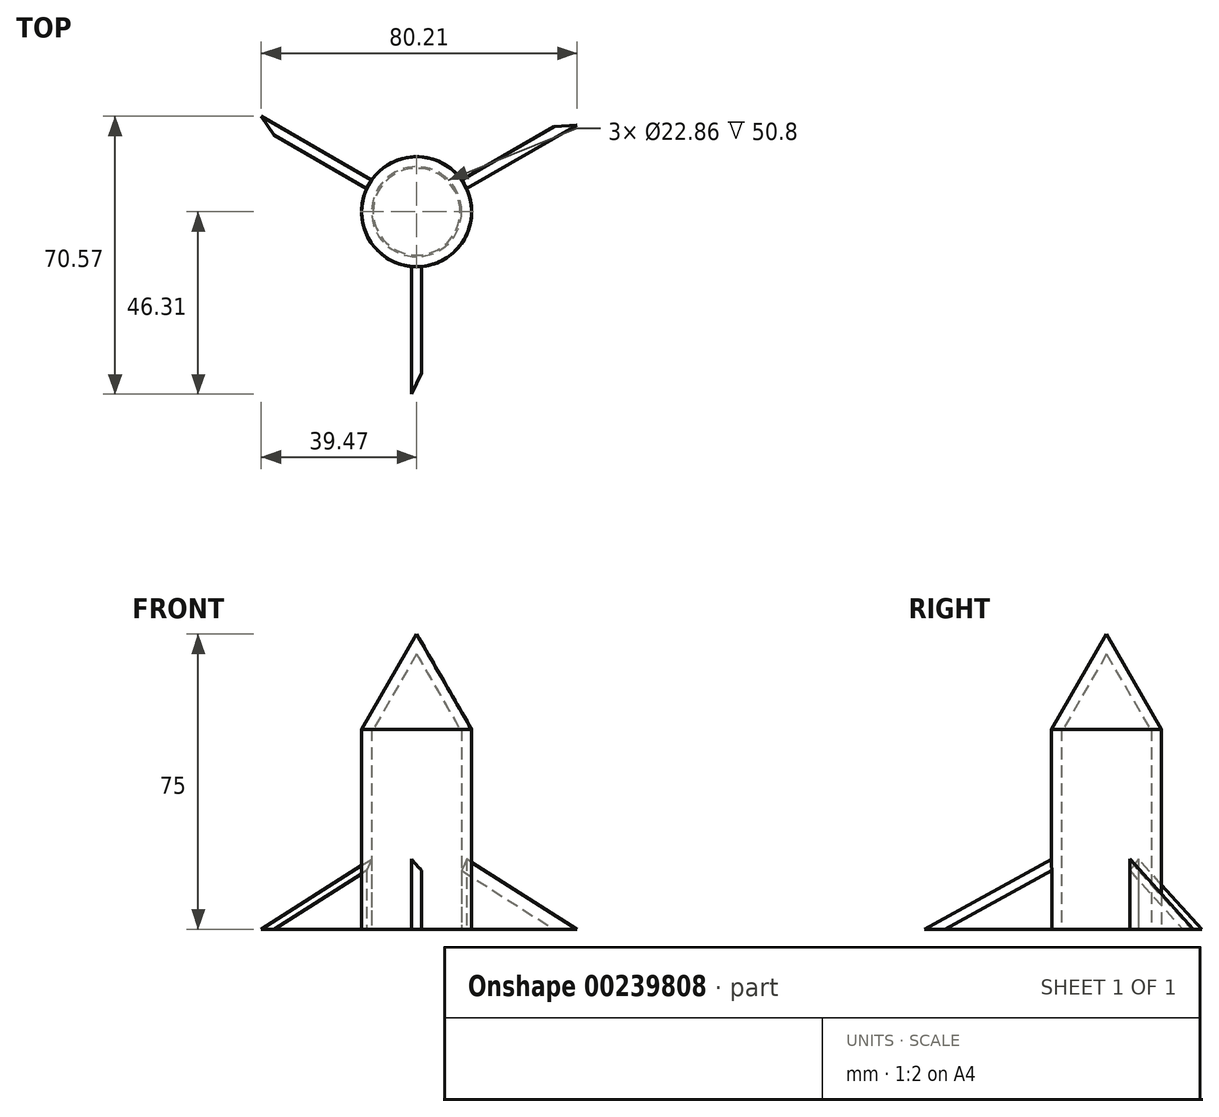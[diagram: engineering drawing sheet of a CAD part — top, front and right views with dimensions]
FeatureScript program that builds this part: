
annotation { "Feature Type Name" : "Feature", "Feature Type Description" : "" }
export const myFeature = defineFeature(function(context is Context, id is Id, definition is map)
    precondition{}
    {
        {
            var Q0;
            Q0=qCreatedBy(makeId("Top.planeOp"),FACE);
            var sketch = newSketch(context, id + "F0", { "sketchPlane" : qUnion([Q0])});
            skCircle(sketch, "E0", {"center": v(0, 0) * mm, "radius": 11.43 * mm});
            skCircle(sketch, "E1", {"center": v(0, 0) * mm, "radius": 13.97 * mm});
            skSolve(sketch);
        }
        {
            var Q0;
            Q0 = qSketchRegion(id + "F0", true);
            extrude(context, id + "F1", {"entities" : qUnion([Q0]), "depth" : 50.8 * mm});
        }
        {
            var Q0;
            Q0=makeQuery(id+"F1.opExtrude","CAP_FACE",FACE,{"disambiguationData":[OSD([sQuery(id+"F0.wireOp",EDGE,"E0"),sQuery(id+"F0.wireOp",EDGE,"E1")])],"isStart":false});
            var sketch = newSketch(context, id + "F2", { "sketchPlane" : qUnion([Q0])});
            skCircle(sketch, "E2.0", {"center": v(0, 0) * mm, "radius": 13.97 * mm});
            skSolve(sketch);
        }
        {
            var Q0;
            Q0 = qSketchRegion(id + "F2", true);
            extrude(context, id + "F3", {"entities" : qUnion([Q0]), "operationType" : NewBodyOperationType.ADD, "depth" : 25.4 * mm, "hasDraft" : true, "draftAngle" : 30 * degree, "draftPullDirection" : true});
        }
        {
            var Q0;
            Q0=makeQuery(id+"F3.opExtrude","CAP_FACE",FACE,{"disambiguationData":[OSD([sQuery(id+"F2.wireOp",EDGE,"E2.0")])],"isStart":true});
            shell(context, id + "F4", {"entities" : qUnion([Q0]), "thickness" : 2.54 * mm});
        }
        {
            var Q0;
            Q0=qCreatedBy(makeId("Right.planeOp"),FACE);
            var sketch = newSketch(context, id + "F5", { "sketchPlane" : qUnion([Q0])});
            skLineSegment(sketch, "E3", {"start": v(-12.63, 0) * mm, "end": v(-12.63, 21.42) * mm});
            skLineSegment(sketch, "E4", {"start": v(-12.63, 21.42) * mm, "end": v(-51.58, 0) * mm});
            skLineSegment(sketch, "E5", {"start": v(-51.58, 0) * mm, "end": v(-12.63, 0) * mm});
            skSolve(sketch);
        }
        {
            var Q0;
            Q0 = qSketchRegion(id + "F5", true);
            extrude(context, id + "F6", {"entities" : qUnion([Q0]), "operationType" : NewBodyOperationType.ADD, "endBound" : BoundingType.SYMMETRIC, "depth" : 2.54 * mm});
        }
        {
            var Q0;
            Q0=makeQuery(id+"F6.opExtrude","CAP_EDGE",EDGE,{"disambiguationData":[OSD([sQuery(id+"F5.wireOp",EDGE,"E4")])],"isStart":false});
            chamfer(context, id + "F7", {"entities" : qUnion([Q0]), "width" : 5.08 * mm, "tangentPropagation" : true});
        }
        {
            var Q0;
            Q0=makeQuery(id+"F1.opExtrude","SWEPT_BODY",BODY,{"disambiguationData":[OSD([sQuery(id+"F0.wireOp",EDGE,"E0"),sQuery(id+"F0.wireOp",EDGE,"E1")])]});
            var Q1;
            Q1=makeQuery(id+"F1.opExtrude","CAP_EDGE",EDGE,{"disambiguationData":[OSD([sQuery(id+"F0.wireOp",EDGE,"E0")])],"isStart":true});
            circularPattern(context, id + "F8", {"entities" : qUnion([Q0]), "axis" : qUnion([Q1]), "angle" : 360 * degree, "instanceCount" : 3, "equalSpace" : true});
        }
    });
